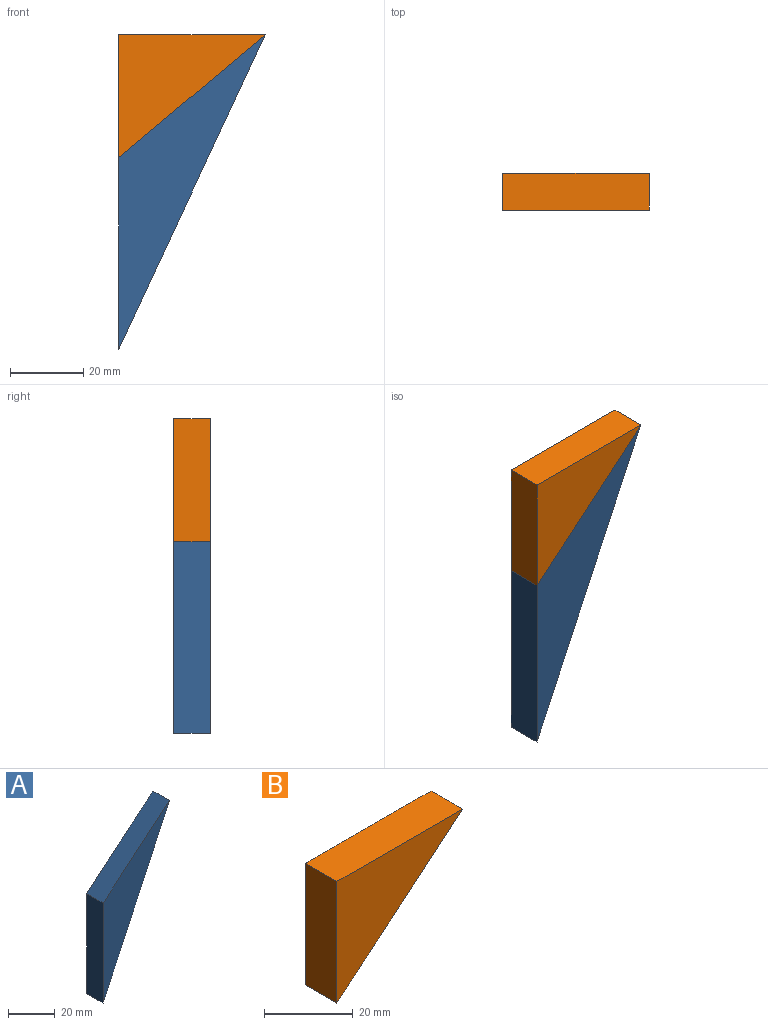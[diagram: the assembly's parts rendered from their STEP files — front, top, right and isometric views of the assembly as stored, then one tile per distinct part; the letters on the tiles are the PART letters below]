
ASSEMBLY  parts=2 mates=1
PART A: 5 faces, bbox 40x10x85.8 mm
  f0: plane 40x33.56mm, normal (-0.64,0,0.77), area 522.2mm2, adj f1,f2,f3,f4
  f1: plane 52.22x10mm, normal (-1,0,0), area 522.2mm2, adj f0,f2,f3,f4
  f2: plane 85.78x40mm, normal (0.91,0,-0.42), area 946.5mm2, adj f0,f1,f3,f4
  f3: plane 85.78x40mm, normal (0,-1,0), area 1044.3mm2, adj f0,f1,f2
  f4: plane 85.78x40mm, normal (0,1,0), area 1044.3mm2, adj f0,f1,f2
PART B: 5 faces, bbox 40x10x33.6 mm
  f0: plane 40x10mm, normal (0,0,1), area 400mm2, adj f1,f2,f3,f4
  f1: plane 33.56x10mm, normal (-1,0,0), area 335.6mm2, adj f0,f2,f3,f4
  f2: plane 40x33.56mm, normal (0.64,0,-0.77), area 522.2mm2, adj f0,f1,f3,f4
  f3: plane 40x33.56mm, normal (0,-1,0), area 671.3mm2, adj f0,f1,f2
  f4: plane 40x33.56mm, normal (0,1,0), area 671.3mm2, adj f0,f1,f2
PLACE A t=(-3.03,6.65,-2.89)mm
PLACE B t=(-3.03,6.65,-2.89)mm
MATE parallel B.f2 <-> A.f0  axis (0.64,0,-0.77) through (16.97,1.65,13.89)mm
